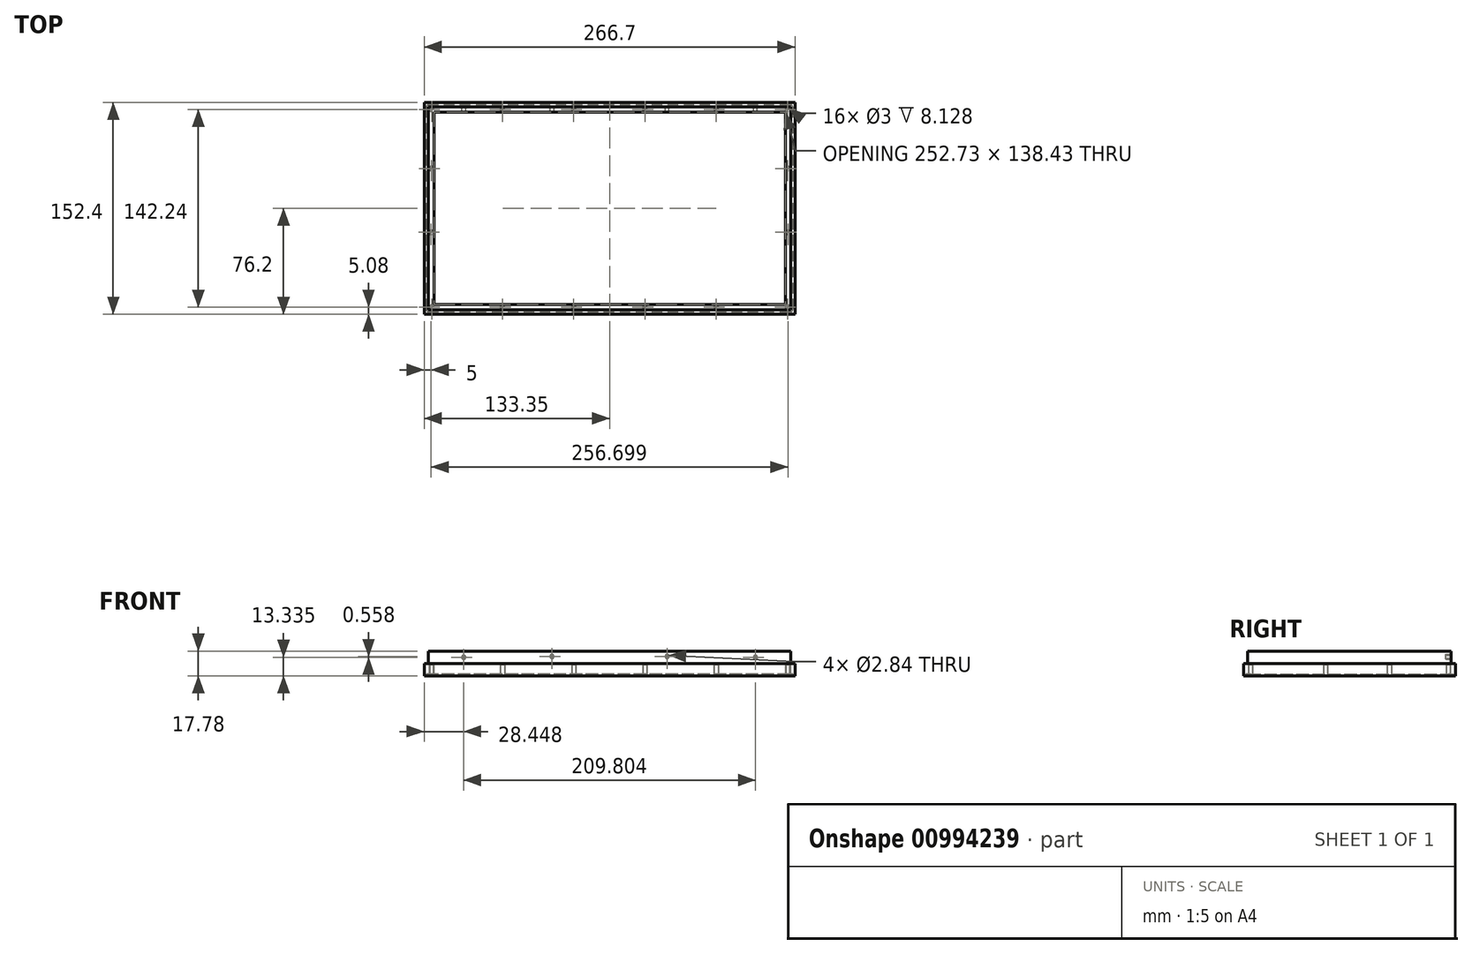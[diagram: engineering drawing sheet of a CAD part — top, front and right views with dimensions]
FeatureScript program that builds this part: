
annotation { "Feature Type Name" : "Feature", "Feature Type Description" : "" }
export const myFeature = defineFeature(function(context is Context, id is Id, definition is map)
    precondition{}
    {
        {
            var Q0;
            Q0=qCreatedBy(makeId("Top.planeOp"),FACE);
            var sketch = newSketch(context, id + "F0", { "sketchPlane" : qUnion([Q0])});
            skLineSegment(sketch, "E0.bottom", {"start": v(133.35, -76.2) * mm, "end": v(-133.35, -76.2) * mm});
            skLineSegment(sketch, "E0.top", {"start": v(133.35, 76.2) * mm, "end": v(-133.35, 76.2) * mm});
            skLineSegment(sketch, "E0.left", {"start": v(133.35, -76.2) * mm, "end": v(133.35, 76.2) * mm});
            skLineSegment(sketch, "E0.right", {"start": v(-133.35, -76.2) * mm, "end": v(-133.35, 76.2) * mm});
            skPoint(sketch, "E0.middle", {"position": v(0, 0) * mm});
            skLineSegment(sketch, "E1.0", {"start": v(126.37, 69.22) * mm, "end": v(-126.37, 69.22) * mm});
            skLineSegment(sketch, "E1.1", {"start": v(126.37, -69.21) * mm, "end": v(126.37, 69.22) * mm});
            skLineSegment(sketch, "E1.2", {"start": v(126.37, -69.21) * mm, "end": v(-126.37, -69.22) * mm});
            skLineSegment(sketch, "E1.3", {"start": v(-126.37, -69.22) * mm, "end": v(-126.37, 69.22) * mm});
            skSolve(sketch);
        }
        {
            var Q0;
            Q0=makeQuery(id+"F0.imprint","IMPRINT",FACE,{"disambiguationData":[TD([[makeQuery(id+"F0.imprint","IMPRINT",EDGE,{"derivedFrom":sQuery(id+"F0.wireOp",EDGE,"E0.bottom")}),-1.0]])]});
            extrude(context, id + "F1", {"entities" : qUnion([Q0]), "depth" : 17.78 * mm, "offsetDistance" : 25.4 * mm});
        }
        {
            var Q0;
            Q0=makeQuery(id+"F1.opExtrude","CAP_FACE",FACE,{"disambiguationData":[OSD([sQuery(id+"F0.wireOp",EDGE,"E0.bottom"),sQuery(id+"F0.wireOp",EDGE,"E0.top"),sQuery(id+"F0.wireOp",EDGE,"E0.left"),sQuery(id+"F0.wireOp",EDGE,"E0.right"),sQuery(id+"F0.wireOp",EDGE,"E1.0"),sQuery(id+"F0.wireOp",EDGE,"E1.1"),sQuery(id+"F0.wireOp",EDGE,"E1.2"),sQuery(id+"F0.wireOp",EDGE,"E1.3")])],"isStart":false});
            var sketch = newSketch(context, id + "F2", { "sketchPlane" : qUnion([Q0])});
            skLineSegment(sketch, "E2.bottom", {"start": v(-133.35, -76.2) * mm, "end": v(133.35, -76.2) * mm});
            skLineSegment(sketch, "E2.top", {"start": v(-133.35, 76.2) * mm, "end": v(133.35, 76.2) * mm});
            skLineSegment(sketch, "E2.left", {"start": v(-133.35, -76.2) * mm, "end": v(-133.35, 76.2) * mm});
            skLineSegment(sketch, "E2.right", {"start": v(133.35, -76.2) * mm, "end": v(133.35, 76.2) * mm});
            skLineSegment(sketch, "E3.0", {"start": v(-130.3, -73.15) * mm, "end": v(-130.3, 73.15) * mm});
            skLineSegment(sketch, "E3.1", {"start": v(-130.3, -73.15) * mm, "end": v(130.3, -73.15) * mm});
            skLineSegment(sketch, "E3.2", {"start": v(130.3, -73.15) * mm, "end": v(130.3, 73.15) * mm});
            skLineSegment(sketch, "E3.3", {"start": v(-130.3, 73.15) * mm, "end": v(130.3, 73.15) * mm});
            skSolve(sketch);
        }
        {
            var Q0;
            Q0=makeQuery(id+"F2.imprint","IMPRINT",FACE,{"disambiguationData":[TD([[makeQuery(id+"F2.imprint","IMPRINT",EDGE,{"derivedFrom":sQuery(id+"F2.wireOp",EDGE,"E2.bottom")}),-1.0]])]});
            extrude(context, id + "F3", {"entities" : qUnion([Q0]), "operationType" : NewBodyOperationType.REMOVE, "oppositeDirection" : true, "depth" : 8.9 * mm, "offsetDistance" : 25.4 * mm});
        }
        {
            var Q0;
            Q0=makeQuery(id+"F1.opExtrude","CAP_FACE",FACE,{"disambiguationData":[OSD([sQuery(id+"F0.wireOp",EDGE,"E0.bottom"),sQuery(id+"F0.wireOp",EDGE,"E0.top"),sQuery(id+"F0.wireOp",EDGE,"E0.left"),sQuery(id+"F0.wireOp",EDGE,"E0.right"),sQuery(id+"F0.wireOp",EDGE,"E1.0"),sQuery(id+"F0.wireOp",EDGE,"E1.1"),sQuery(id+"F0.wireOp",EDGE,"E1.2"),sQuery(id+"F0.wireOp",EDGE,"E1.3")])],"isStart":true});
            var sketch = newSketch(context, id + "F4", { "sketchPlane" : qUnion([Q0])});
            skLineSegment(sketch, "E4.bottom", {"start": v(131.75, 74.6) * mm, "end": v(-131.75, 74.6) * mm});
            skLineSegment(sketch, "E4.top", {"start": v(131.75, -74.6) * mm, "end": v(-131.75, -74.6) * mm});
            skLineSegment(sketch, "E4.left", {"start": v(131.75, 74.6) * mm, "end": v(131.75, -74.6) * mm});
            skLineSegment(sketch, "E4.right", {"start": v(-131.75, 74.6) * mm, "end": v(-131.75, -74.6) * mm});
            skPoint(sketch, "E4.middle", {"position": v(0, 0) * mm});
            skLineSegment(sketch, "E5.bottom", {"start": v(130.18, 73.02) * mm, "end": v(-130.18, 73.03) * mm});
            skLineSegment(sketch, "E5.top", {"start": v(130.18, -73.03) * mm, "end": v(-130.18, -73.02) * mm});
            skLineSegment(sketch, "E5.left", {"start": v(130.18, 73.02) * mm, "end": v(130.18, -73.03) * mm});
            skLineSegment(sketch, "E5.right", {"start": v(-130.18, 73.03) * mm, "end": v(-130.18, -73.02) * mm});
            skSolve(sketch);
        }
        {
            var Q0;
            Q0=makeQuery(id+"F4.imprint","IMPRINT",FACE,{"disambiguationData":[TD([[makeQuery(id+"F4.imprint","IMPRINT",EDGE,{"derivedFrom":sQuery(id+"F4.wireOp",EDGE,"E4.bottom")}),1.0]])]});
            extrude(context, id + "F5", {"entities" : qUnion([Q0]), "operationType" : NewBodyOperationType.REMOVE, "oppositeDirection" : true, "depth" : 1.27 * mm, "offsetDistance" : 25.4 * mm});
        }
        {
            var Q0;
            Q0=makeQuery(id+"F1.opExtrude","SWEPT_EDGE",EDGE,{"disambiguationData":[OSD([sQuery(id+"F0.wireOp",EDGE,"E1.2"),sQuery(id+"F0.wireOp",EDGE,"E1.3")])]});
            var Q1;
            Q1=makeQuery(id+"F1.opExtrude","SWEPT_EDGE",EDGE,{"disambiguationData":[OSD([sQuery(id+"F0.wireOp",EDGE,"E1.1"),sQuery(id+"F0.wireOp",EDGE,"E1.2")])]});
            var Q2;
            Q2=makeQuery(id+"F1.opExtrude","SWEPT_EDGE",EDGE,{"disambiguationData":[OSD([sQuery(id+"F0.wireOp",EDGE,"E1.0"),sQuery(id+"F0.wireOp",EDGE,"E1.1")])]});
            var Q3;
            Q3=makeQuery(id+"F1.opExtrude","SWEPT_EDGE",EDGE,{"disambiguationData":[OSD([sQuery(id+"F0.wireOp",EDGE,"E1.0"),sQuery(id+"F0.wireOp",EDGE,"E1.3")])]});
            fillet(context, id + "F6", {"entities" : qUnion([Q0, Q1, Q2, Q3]), "radius" : 0.76 * mm, "tangentPropagation" : true, "allowEdgeOverflow" : false});
        }
        {
            var Q0;
            Q0=makeQuery(id+"F5.boolean.opBoolean","COPY",EDGE,{"derivedFrom":makeQuery(id+"F5.opExtrude","SWEPT_EDGE",EDGE,{"disambiguationData":[OSD([sQuery(id+"F4.wireOp",EDGE,"E5.top"),sQuery(id+"F4.wireOp",EDGE,"E5.left")])]})});
            var Q1;
            Q1=makeQuery(id+"F5.boolean.opBoolean","COPY",EDGE,{"derivedFrom":makeQuery(id+"F5.opExtrude","SWEPT_EDGE",EDGE,{"disambiguationData":[OSD([sQuery(id+"F4.wireOp",EDGE,"E4.top"),sQuery(id+"F4.wireOp",EDGE,"E4.left")])]})});
            var Q2;
            Q2=makeQuery(id+"F5.boolean.opBoolean","COPY",EDGE,{"derivedFrom":makeQuery(id+"F5.opExtrude","SWEPT_EDGE",EDGE,{"disambiguationData":[OSD([sQuery(id+"F4.wireOp",EDGE,"E5.top"),sQuery(id+"F4.wireOp",EDGE,"E5.right")])]})});
            var Q3;
            Q3=makeQuery(id+"F5.boolean.opBoolean","COPY",EDGE,{"derivedFrom":makeQuery(id+"F5.opExtrude","SWEPT_EDGE",EDGE,{"disambiguationData":[OSD([sQuery(id+"F4.wireOp",EDGE,"E4.top"),sQuery(id+"F4.wireOp",EDGE,"E4.right")])]})});
            var Q4;
            Q4=makeQuery(id+"F5.boolean.opBoolean","COPY",EDGE,{"derivedFrom":makeQuery(id+"F5.opExtrude","SWEPT_EDGE",EDGE,{"disambiguationData":[OSD([sQuery(id+"F4.wireOp",EDGE,"E5.bottom"),sQuery(id+"F4.wireOp",EDGE,"E5.right")])]})});
            var Q5;
            Q5=makeQuery(id+"F5.boolean.opBoolean","COPY",EDGE,{"derivedFrom":makeQuery(id+"F5.opExtrude","SWEPT_EDGE",EDGE,{"disambiguationData":[OSD([sQuery(id+"F4.wireOp",EDGE,"E4.bottom"),sQuery(id+"F4.wireOp",EDGE,"E4.right")])]})});
            var Q6;
            Q6=makeQuery(id+"F5.boolean.opBoolean","COPY",EDGE,{"derivedFrom":makeQuery(id+"F5.opExtrude","SWEPT_EDGE",EDGE,{"disambiguationData":[OSD([sQuery(id+"F4.wireOp",EDGE,"E5.bottom"),sQuery(id+"F4.wireOp",EDGE,"E5.left")])]})});
            var Q7;
            Q7=makeQuery(id+"F5.boolean.opBoolean","COPY",EDGE,{"derivedFrom":makeQuery(id+"F5.opExtrude","SWEPT_EDGE",EDGE,{"disambiguationData":[OSD([sQuery(id+"F4.wireOp",EDGE,"E4.bottom"),sQuery(id+"F4.wireOp",EDGE,"E4.left")])]})});
            fillet(context, id + "F7", {"entities" : qUnion([Q0, Q1, Q2, Q3, Q4, Q5, Q6, Q7]), "radius" : 1.9 * mm, "tangentPropagation" : true, "allowEdgeOverflow" : false});
        }
        {
            var Q0;
            {var subQ0=sQuery(id+"F0.wireOp",EDGE,"E1.3");var subQ1=sQuery(id+"F0.wireOp",EDGE,"E1.2");var subQ2=sQuery(id+"F0.wireOp",EDGE,"E1.1");var subQ3=sQuery(id+"F0.wireOp",EDGE,"E1.0");Q0=makeQuery(id+"F5.boolean.opBoolean","SPLIT",FACE,{"disambiguationData":[TD([makeQuery(id+"F1.opExtrude","SWEPT_FACE",FACE,{"disambiguationData":[OSD([subQ3])]})])],"derivedFrom":makeQuery(id+"F1.opExtrude","CAP_FACE",FACE,{"disambiguationData":[OSD([sQuery(id+"F0.wireOp",EDGE,"E0.bottom"),sQuery(id+"F0.wireOp",EDGE,"E0.top"),sQuery(id+"F0.wireOp",EDGE,"E0.left"),sQuery(id+"F0.wireOp",EDGE,"E0.right"),subQ3,subQ2,subQ1,subQ0])],"isStart":true})});}
            var sketch = newSketch(context, id + "F8", { "sketchPlane" : qUnion([Q0])});
            skCircle(sketch, "E6", {"center": v(127.95, -71.12) * mm, "radius": 1.5 * mm});
            skLineSegment(sketch, "E7", {"start": v(127.8, -102.4) * mm, "end": v(127.95, -71.12) * mm, "construction": true});
            skCircle(sketch, "E8", {"center": v(128.14, -28.64) * mm, "radius": 1.5 * mm});
            skCircle(sketch, "E9", {"center": v(128.35, 17.28) * mm, "radius": 1.5 * mm});
            skCircle(sketch, "E10.MirrorC", {"center": v(-127.95, -71.12) * mm, "radius": 1.5 * mm});
            skCircle(sketch, "E11.MirrorC", {"center": v(-128.35, 17.28) * mm, "radius": 1.5 * mm});
            skCircle(sketch, "E12.MirrorC", {"center": v(-128.14, -28.64) * mm, "radius": 1.5 * mm});
            skLineSegment(sketch, "E13.MirrorCS", {"start": v(-127.8, -102.4) * mm, "end": v(-127.95, -71.12) * mm, "construction": true});
            skLineSegment(sketch, "E14.1.0.0", {"start": v(76.55, -102.4) * mm, "end": v(76.7, -71.12) * mm, "construction": true});
            skCircle(sketch, "E14.1.0.3", {"center": v(76.7, -71.12) * mm, "radius": 1.5 * mm});
            skLineSegment(sketch, "E14.2.0.0", {"start": v(25.3, -102.4) * mm, "end": v(25.43, -71.12) * mm, "construction": true});
            skCircle(sketch, "E14.2.0.3", {"center": v(25.43, -71.12) * mm, "radius": 1.5 * mm});
            skLineSegment(sketch, "E14.3.0.0", {"start": v(-25.96, -102.4) * mm, "end": v(-25.82, -71.12) * mm, "construction": true});
            skCircle(sketch, "E14.3.0.3", {"center": v(-25.82, -71.12) * mm, "radius": 1.5 * mm});
            skLineSegment(sketch, "E14.4.0.0", {"start": v(-77.22, -102.4) * mm, "end": v(-77.08, -71.12) * mm, "construction": true});
            skCircle(sketch, "E14.4.0.3", {"center": v(-77.08, -71.12) * mm, "radius": 1.5 * mm});
            skLineSegment(sketch, "E14.direction1", {"start": v(127.95, -71.12) * mm, "end": v(76.7, -71.12) * mm, "construction": true});
            skCircle(sketch, "E15.MirrorC", {"center": v(76.7, 71.12) * mm, "radius": 1.5 * mm});
            skCircle(sketch, "E16.MirrorC", {"center": v(127.95, 71.12) * mm, "radius": 1.5 * mm});
            skCircle(sketch, "E17.MirrorC", {"center": v(-127.95, 71.12) * mm, "radius": 1.5 * mm});
            skCircle(sketch, "E18.MirrorC", {"center": v(25.43, 71.12) * mm, "radius": 1.5 * mm});
            skCircle(sketch, "E19.MirrorC", {"center": v(-77.08, 71.12) * mm, "radius": 1.5 * mm});
            skCircle(sketch, "E20.MirrorC", {"center": v(-25.82, 71.12) * mm, "radius": 1.5 * mm});
            skLineSegment(sketch, "E21.MirrorCS", {"start": v(127.95, 71.12) * mm, "end": v(76.7, 71.12) * mm, "construction": true});
            skSolve(sketch);
        }
        {
            var Q0;
            Q0 = qSketchRegion(id + "F8", true);
            extrude(context, id + "F9", {"entities" : qUnion([Q0]), "operationType" : NewBodyOperationType.REMOVE, "oppositeDirection" : true, "depth" : 8.13 * mm, "offsetDistance" : 25.4 * mm});
        }
        {
            var Q0;
            Q0=makeQuery(id+"F3.boolean.opBoolean","COPY",FACE,{"derivedFrom":makeQuery(id+"F3.opExtrude","SWEPT_FACE",FACE,{"disambiguationData":[OSD([sQuery(id+"F2.wireOp",EDGE,"E3.3")])]})});
            var sketch = newSketch(context, id + "F10", { "sketchPlane" : qUnion([Q0])});
            skCircle(sketch, "E22", {"center": v(-104.9, 13.33) * mm, "radius": 1.42 * mm});
            skPoint(sketch, "E22.centerSnap0", {"position": v(-130.3, 13.33) * mm});
            skCircle(sketch, "E23", {"center": v(-41.4, 13.9) * mm, "radius": 1.42 * mm});
            skCircle(sketch, "E24.MirrorC", {"center": v(104.9, 13.33) * mm, "radius": 1.42 * mm});
            skCircle(sketch, "E25.MirrorC", {"center": v(41.4, 13.9) * mm, "radius": 1.42 * mm});
            skSolve(sketch);
        }
        {
            var Q0;
            Q0 = qSketchRegion(id + "F10", true);
            extrude(context, id + "F11", {"entities" : qUnion([Q0]), "operationType" : NewBodyOperationType.REMOVE, "oppositeDirection" : true, "depth" : 25.4 * mm, "offsetDistance" : 25.4 * mm});
        }
    });
